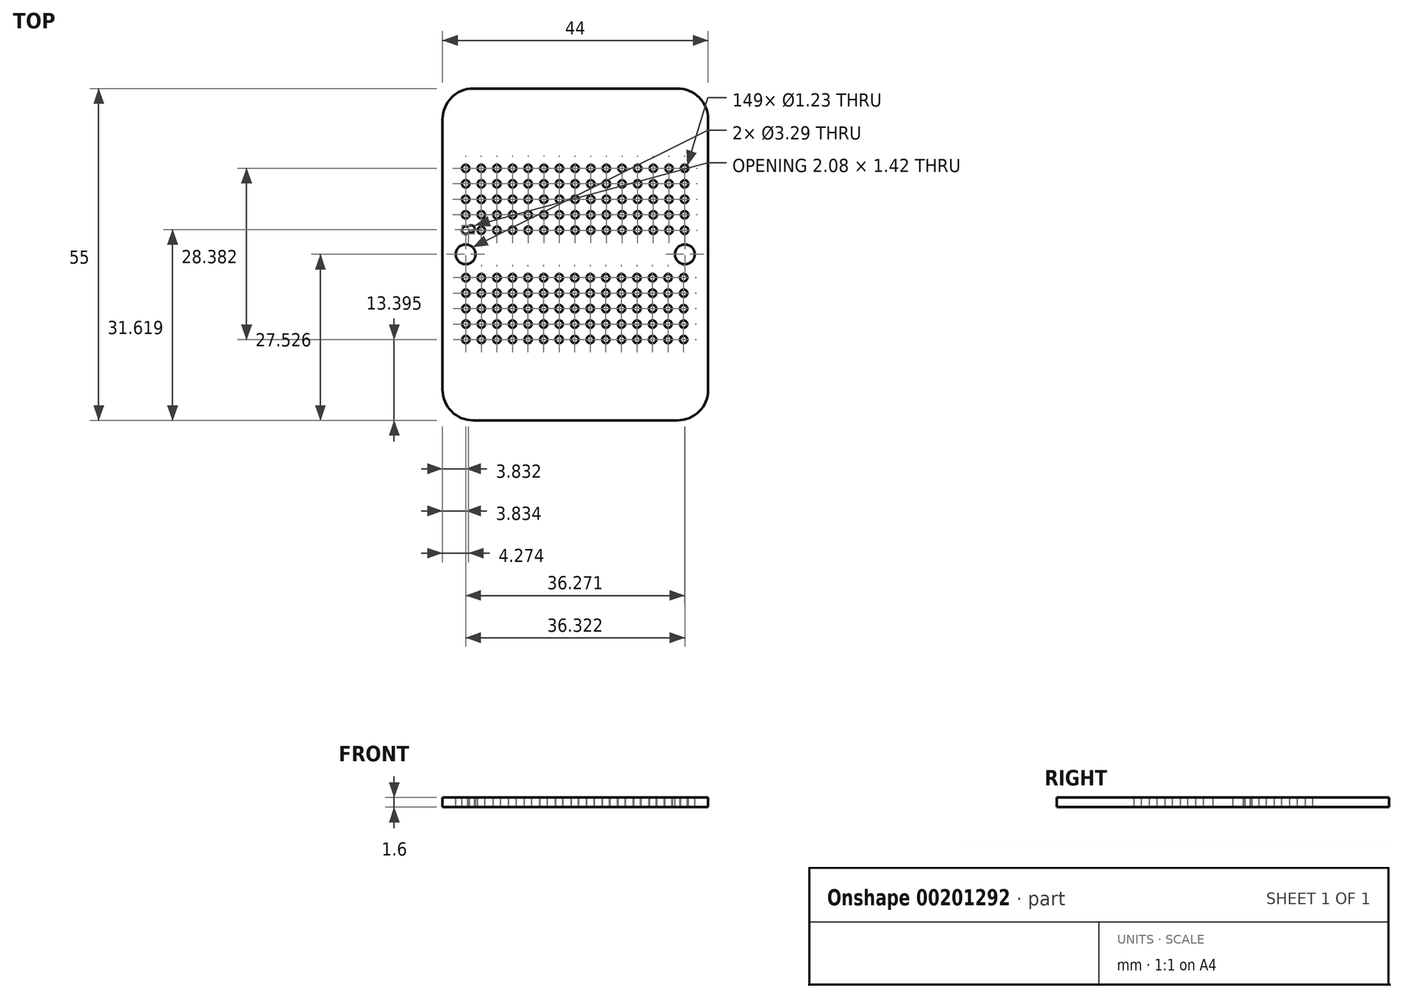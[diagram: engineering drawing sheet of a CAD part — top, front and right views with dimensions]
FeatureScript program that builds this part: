
annotation { "Feature Type Name" : "Feature", "Feature Type Description" : "" }
export const myFeature = defineFeature(function(context is Context, id is Id, definition is map)
    precondition{}
    {
        {
            var Q0;
            Q0=qCreatedBy(makeId("Top.planeOp"),FACE);
            var sketch = newSketch(context, id + "F0", { "sketchPlane" : qUnion([Q0])});
            skLineSegment(sketch, "E0.bottom", {"start": v(0, 0) * mm, "end": v(44, 0) * mm});
            skLineSegment(sketch, "E0.top", {"start": v(0, -55) * mm, "end": v(44, -55) * mm});
            skLineSegment(sketch, "E0.left", {"start": v(0, 0) * mm, "end": v(0, -55) * mm});
            skLineSegment(sketch, "E0.right", {"start": v(44, 0) * mm, "end": v(44, -55) * mm});
            skSolve(sketch);
        }
        {
            var Q0;
            Q0=makeQuery(id+"F0.imprint","IMPRINT",FACE,{"disambiguationData":[TD([[makeQuery(id+"F0.imprint","IMPRINT",EDGE,{"derivedFrom":sQuery(id+"F0.wireOp",EDGE,"E0.bottom")}),-1.0]])]});
            extrude(context, id + "F1", {"entities" : qUnion([Q0]), "depth" : 1.6 * mm});
        }
        {
            var Q0;
            Q0=makeQuery(id+"F1.opExtrude","SWEPT_EDGE",EDGE,{"disambiguationData":[OSD([sQuery(id+"F0.wireOp",EDGE,"E0.top"),sQuery(id+"F0.wireOp",EDGE,"E0.left")])]});
            var Q1;
            Q1=makeQuery(id+"F1.opExtrude","SWEPT_EDGE",EDGE,{"disambiguationData":[OSD([sQuery(id+"F0.wireOp",EDGE,"E0.top"),sQuery(id+"F0.wireOp",EDGE,"E0.right")])]});
            var Q2;
            Q2=makeQuery(id+"F1.opExtrude","SWEPT_EDGE",EDGE,{"disambiguationData":[OSD([sQuery(id+"F0.wireOp",EDGE,"E0.bottom"),sQuery(id+"F0.wireOp",EDGE,"E0.right")])]});
            var Q3;
            Q3=makeQuery(id+"F1.opExtrude","SWEPT_EDGE",EDGE,{"disambiguationData":[OSD([sQuery(id+"F0.wireOp",EDGE,"E0.bottom"),sQuery(id+"F0.wireOp",EDGE,"E0.left")])]});
            fillet(context, id + "F2", {"entities" : qUnion([Q0, Q1, Q2, Q3]), "radius" : 5.08 * mm, "tangentPropagation" : true, "allowEdgeOverflow" : false});
        }
        {
            var Q0;
            Q0=makeQuery(id+"F1.opExtrude","CAP_FACE",FACE,{"disambiguationData":[OSD([sQuery(id+"F0.wireOp",EDGE,"E0.bottom"),sQuery(id+"F0.wireOp",EDGE,"E0.top"),sQuery(id+"F0.wireOp",EDGE,"E0.left"),sQuery(id+"F0.wireOp",EDGE,"E0.right")])],"isStart":false});
            var sketch = newSketch(context, id + "F3", { "sketchPlane" : qUnion([Q0])});
            skCircle(sketch, "E1", {"center": v(3.83, -27.47) * mm, "radius": 1.65 * mm});
            skCircle(sketch, "E2.1.0.0", {"center": v(40.16, -27.47) * mm, "radius": 1.65 * mm});
            skLineSegment(sketch, "E2.direction1", {"start": v(3.83, -27.47) * mm, "end": v(40.16, -27.47) * mm, "construction": true});
            skCircle(sketch, "E3", {"center": v(3.83, -13.22) * mm, "radius": 0.61 * mm});
            skCircle(sketch, "E4.0.1.0", {"center": v(3.83, -15.79) * mm, "radius": 0.61 * mm});
            skCircle(sketch, "E4.0.2.0", {"center": v(3.83, -18.35) * mm, "radius": 0.61 * mm});
            skCircle(sketch, "E4.0.3.0", {"center": v(3.83, -20.92) * mm, "radius": 0.61 * mm});
            skCircle(sketch, "E4.0.4.0", {"center": v(3.83, -23.49) * mm, "radius": 0.61 * mm});
            skCircle(sketch, "E4.1.0.0", {"center": v(6.42, -13.22) * mm, "radius": 0.61 * mm});
            skCircle(sketch, "E4.1.1.0", {"center": v(6.42, -15.79) * mm, "radius": 0.61 * mm});
            skCircle(sketch, "E4.1.2.0", {"center": v(6.42, -18.35) * mm, "radius": 0.61 * mm});
            skCircle(sketch, "E4.1.3.0", {"center": v(6.42, -20.92) * mm, "radius": 0.61 * mm});
            skCircle(sketch, "E4.1.4.0", {"center": v(6.42, -23.49) * mm, "radius": 0.61 * mm});
            skCircle(sketch, "E4.2.0.0", {"center": v(9.01, -13.22) * mm, "radius": 0.61 * mm});
            skCircle(sketch, "E4.2.1.0", {"center": v(9.01, -15.79) * mm, "radius": 0.61 * mm});
            skCircle(sketch, "E4.2.2.0", {"center": v(9.01, -18.35) * mm, "radius": 0.61 * mm});
            skCircle(sketch, "E4.2.3.0", {"center": v(9.01, -20.92) * mm, "radius": 0.61 * mm});
            skCircle(sketch, "E4.2.4.0", {"center": v(9.01, -23.49) * mm, "radius": 0.61 * mm});
            skCircle(sketch, "E4.3.0.0", {"center": v(11.6, -13.22) * mm, "radius": 0.61 * mm});
            skCircle(sketch, "E4.3.1.0", {"center": v(11.6, -15.79) * mm, "radius": 0.61 * mm});
            skCircle(sketch, "E4.3.2.0", {"center": v(11.6, -18.35) * mm, "radius": 0.61 * mm});
            skCircle(sketch, "E4.3.3.0", {"center": v(11.6, -20.92) * mm, "radius": 0.61 * mm});
            skCircle(sketch, "E4.3.4.0", {"center": v(11.6, -23.49) * mm, "radius": 0.61 * mm});
            skCircle(sketch, "E4.4.0.0", {"center": v(14.2, -13.22) * mm, "radius": 0.61 * mm});
            skCircle(sketch, "E4.4.1.0", {"center": v(14.2, -15.79) * mm, "radius": 0.61 * mm});
            skCircle(sketch, "E4.4.2.0", {"center": v(14.2, -18.35) * mm, "radius": 0.61 * mm});
            skCircle(sketch, "E4.4.3.0", {"center": v(14.2, -20.92) * mm, "radius": 0.61 * mm});
            skCircle(sketch, "E4.4.4.0", {"center": v(14.2, -23.49) * mm, "radius": 0.61 * mm});
            skCircle(sketch, "E4.5.0.0", {"center": v(16.79, -13.22) * mm, "radius": 0.61 * mm});
            skCircle(sketch, "E4.5.1.0", {"center": v(16.79, -15.79) * mm, "radius": 0.61 * mm});
            skCircle(sketch, "E4.5.2.0", {"center": v(16.79, -18.35) * mm, "radius": 0.61 * mm});
            skCircle(sketch, "E4.5.3.0", {"center": v(16.79, -20.92) * mm, "radius": 0.61 * mm});
            skCircle(sketch, "E4.5.4.0", {"center": v(16.79, -23.49) * mm, "radius": 0.61 * mm});
            skCircle(sketch, "E4.6.0.0", {"center": v(19.38, -13.22) * mm, "radius": 0.61 * mm});
            skCircle(sketch, "E4.6.1.0", {"center": v(19.38, -15.79) * mm, "radius": 0.61 * mm});
            skCircle(sketch, "E4.6.2.0", {"center": v(19.38, -18.35) * mm, "radius": 0.61 * mm});
            skCircle(sketch, "E4.6.3.0", {"center": v(19.38, -20.92) * mm, "radius": 0.61 * mm});
            skCircle(sketch, "E4.6.4.0", {"center": v(19.38, -23.49) * mm, "radius": 0.61 * mm});
            skCircle(sketch, "E4.7.0.0", {"center": v(21.97, -13.22) * mm, "radius": 0.61 * mm});
            skCircle(sketch, "E4.7.1.0", {"center": v(21.97, -15.79) * mm, "radius": 0.61 * mm});
            skCircle(sketch, "E4.7.2.0", {"center": v(21.97, -18.35) * mm, "radius": 0.61 * mm});
            skCircle(sketch, "E4.7.3.0", {"center": v(21.97, -20.92) * mm, "radius": 0.61 * mm});
            skCircle(sketch, "E4.7.4.0", {"center": v(21.97, -23.49) * mm, "radius": 0.61 * mm});
            skCircle(sketch, "E4.8.0.0", {"center": v(24.56, -13.22) * mm, "radius": 0.61 * mm});
            skCircle(sketch, "E4.8.1.0", {"center": v(24.56, -15.79) * mm, "radius": 0.61 * mm});
            skCircle(sketch, "E4.8.2.0", {"center": v(24.56, -18.35) * mm, "radius": 0.61 * mm});
            skCircle(sketch, "E4.8.3.0", {"center": v(24.56, -20.92) * mm, "radius": 0.61 * mm});
            skCircle(sketch, "E4.8.4.0", {"center": v(24.56, -23.49) * mm, "radius": 0.61 * mm});
            skCircle(sketch, "E4.9.0.0", {"center": v(27.15, -13.22) * mm, "radius": 0.61 * mm});
            skCircle(sketch, "E4.9.1.0", {"center": v(27.15, -15.79) * mm, "radius": 0.61 * mm});
            skCircle(sketch, "E4.9.2.0", {"center": v(27.15, -18.35) * mm, "radius": 0.61 * mm});
            skCircle(sketch, "E4.9.3.0", {"center": v(27.15, -20.92) * mm, "radius": 0.61 * mm});
            skCircle(sketch, "E4.9.4.0", {"center": v(27.15, -23.49) * mm, "radius": 0.61 * mm});
            skCircle(sketch, "E4.10.0.0", {"center": v(29.74, -13.22) * mm, "radius": 0.61 * mm});
            skCircle(sketch, "E4.10.1.0", {"center": v(29.74, -15.79) * mm, "radius": 0.61 * mm});
            skCircle(sketch, "E4.10.2.0", {"center": v(29.74, -18.35) * mm, "radius": 0.61 * mm});
            skCircle(sketch, "E4.10.3.0", {"center": v(29.74, -20.92) * mm, "radius": 0.61 * mm});
            skCircle(sketch, "E4.10.4.0", {"center": v(29.74, -23.49) * mm, "radius": 0.61 * mm});
            skCircle(sketch, "E4.11.0.0", {"center": v(32.33, -13.22) * mm, "radius": 0.61 * mm});
            skCircle(sketch, "E4.11.1.0", {"center": v(32.33, -15.79) * mm, "radius": 0.61 * mm});
            skCircle(sketch, "E4.11.2.0", {"center": v(32.33, -18.35) * mm, "radius": 0.61 * mm});
            skCircle(sketch, "E4.11.3.0", {"center": v(32.33, -20.92) * mm, "radius": 0.61 * mm});
            skCircle(sketch, "E4.11.4.0", {"center": v(32.33, -23.49) * mm, "radius": 0.61 * mm});
            skCircle(sketch, "E4.12.0.0", {"center": v(34.92, -13.22) * mm, "radius": 0.61 * mm});
            skCircle(sketch, "E4.12.1.0", {"center": v(34.92, -15.79) * mm, "radius": 0.61 * mm});
            skCircle(sketch, "E4.12.2.0", {"center": v(34.92, -18.35) * mm, "radius": 0.61 * mm});
            skCircle(sketch, "E4.12.3.0", {"center": v(34.92, -20.92) * mm, "radius": 0.61 * mm});
            skCircle(sketch, "E4.12.4.0", {"center": v(34.92, -23.49) * mm, "radius": 0.61 * mm});
            skCircle(sketch, "E4.13.0.0", {"center": v(37.51, -13.22) * mm, "radius": 0.61 * mm});
            skCircle(sketch, "E4.13.1.0", {"center": v(37.51, -15.79) * mm, "radius": 0.61 * mm});
            skCircle(sketch, "E4.13.2.0", {"center": v(37.51, -18.35) * mm, "radius": 0.61 * mm});
            skCircle(sketch, "E4.13.3.0", {"center": v(37.51, -20.92) * mm, "radius": 0.61 * mm});
            skCircle(sketch, "E4.13.4.0", {"center": v(37.51, -23.49) * mm, "radius": 0.61 * mm});
            skCircle(sketch, "E4.14.0.0", {"center": v(40.1, -13.22) * mm, "radius": 0.61 * mm});
            skCircle(sketch, "E4.14.1.0", {"center": v(40.1, -15.79) * mm, "radius": 0.61 * mm});
            skCircle(sketch, "E4.14.2.0", {"center": v(40.1, -18.35) * mm, "radius": 0.61 * mm});
            skCircle(sketch, "E4.14.3.0", {"center": v(40.1, -20.92) * mm, "radius": 0.61 * mm});
            skCircle(sketch, "E4.14.4.0", {"center": v(40.1, -23.49) * mm, "radius": 0.61 * mm});
            skLineSegment(sketch, "E4.direction1", {"start": v(3.83, -13.22) * mm, "end": v(6.42, -13.22) * mm, "construction": true});
            skLineSegment(sketch, "E4.direction2", {"start": v(3.83, -13.22) * mm, "end": v(3.83, -15.79) * mm, "construction": true});
            skCircle(sketch, "E5", {"center": v(4.72, -23.28) * mm, "radius": 0.61 * mm});
            skCircle(sketch, "E6", {"center": v(3.86, -31.34) * mm, "radius": 0.61 * mm});
            skCircle(sketch, "E7.0.1.0", {"center": v(3.86, -33.9) * mm, "radius": 0.61 * mm});
            skCircle(sketch, "E7.0.2.0", {"center": v(3.86, -36.47) * mm, "radius": 0.61 * mm});
            skCircle(sketch, "E7.0.3.0", {"center": v(3.86, -39.04) * mm, "radius": 0.61 * mm});
            skCircle(sketch, "E7.0.4.0", {"center": v(3.86, -41.6) * mm, "radius": 0.61 * mm});
            skCircle(sketch, "E7.1.0.0", {"center": v(6.43, -31.34) * mm, "radius": 0.61 * mm});
            skCircle(sketch, "E7.1.1.0", {"center": v(6.43, -33.9) * mm, "radius": 0.61 * mm});
            skCircle(sketch, "E7.1.2.0", {"center": v(6.43, -36.47) * mm, "radius": 0.61 * mm});
            skCircle(sketch, "E7.1.3.0", {"center": v(6.43, -39.04) * mm, "radius": 0.61 * mm});
            skCircle(sketch, "E7.1.4.0", {"center": v(6.43, -41.6) * mm, "radius": 0.61 * mm});
            skCircle(sketch, "E7.2.0.0", {"center": v(9.01, -31.34) * mm, "radius": 0.61 * mm});
            skCircle(sketch, "E7.2.1.0", {"center": v(9.01, -33.9) * mm, "radius": 0.61 * mm});
            skCircle(sketch, "E7.2.2.0", {"center": v(9.01, -36.47) * mm, "radius": 0.61 * mm});
            skCircle(sketch, "E7.2.3.0", {"center": v(9.01, -39.04) * mm, "radius": 0.61 * mm});
            skCircle(sketch, "E7.2.4.0", {"center": v(9.01, -41.6) * mm, "radius": 0.61 * mm});
            skCircle(sketch, "E7.3.0.0", {"center": v(11.6, -31.34) * mm, "radius": 0.61 * mm});
            skCircle(sketch, "E7.3.1.0", {"center": v(11.6, -33.9) * mm, "radius": 0.61 * mm});
            skCircle(sketch, "E7.3.2.0", {"center": v(11.6, -36.47) * mm, "radius": 0.61 * mm});
            skCircle(sketch, "E7.3.3.0", {"center": v(11.6, -39.04) * mm, "radius": 0.61 * mm});
            skCircle(sketch, "E7.3.4.0", {"center": v(11.6, -41.6) * mm, "radius": 0.61 * mm});
            skCircle(sketch, "E7.4.0.0", {"center": v(14.17, -31.34) * mm, "radius": 0.61 * mm});
            skCircle(sketch, "E7.4.1.0", {"center": v(14.17, -33.9) * mm, "radius": 0.61 * mm});
            skCircle(sketch, "E7.4.2.0", {"center": v(14.17, -36.47) * mm, "radius": 0.61 * mm});
            skCircle(sketch, "E7.4.3.0", {"center": v(14.17, -39.04) * mm, "radius": 0.61 * mm});
            skCircle(sketch, "E7.4.4.0", {"center": v(14.17, -41.6) * mm, "radius": 0.61 * mm});
            skCircle(sketch, "E7.5.0.0", {"center": v(16.75, -31.34) * mm, "radius": 0.61 * mm});
            skCircle(sketch, "E7.5.1.0", {"center": v(16.75, -33.9) * mm, "radius": 0.61 * mm});
            skCircle(sketch, "E7.5.2.0", {"center": v(16.75, -36.47) * mm, "radius": 0.61 * mm});
            skCircle(sketch, "E7.5.3.0", {"center": v(16.75, -39.04) * mm, "radius": 0.61 * mm});
            skCircle(sketch, "E7.5.4.0", {"center": v(16.75, -41.6) * mm, "radius": 0.61 * mm});
            skCircle(sketch, "E7.6.0.0", {"center": v(19.32, -31.34) * mm, "radius": 0.61 * mm});
            skCircle(sketch, "E7.6.1.0", {"center": v(19.32, -33.9) * mm, "radius": 0.61 * mm});
            skCircle(sketch, "E7.6.2.0", {"center": v(19.32, -36.47) * mm, "radius": 0.61 * mm});
            skCircle(sketch, "E7.6.3.0", {"center": v(19.32, -39.04) * mm, "radius": 0.61 * mm});
            skCircle(sketch, "E7.6.4.0", {"center": v(19.32, -41.6) * mm, "radius": 0.61 * mm});
            skCircle(sketch, "E7.7.0.0", {"center": v(21.9, -31.34) * mm, "radius": 0.61 * mm});
            skCircle(sketch, "E7.7.1.0", {"center": v(21.9, -33.9) * mm, "radius": 0.61 * mm});
            skCircle(sketch, "E7.7.2.0", {"center": v(21.9, -36.47) * mm, "radius": 0.61 * mm});
            skCircle(sketch, "E7.7.3.0", {"center": v(21.9, -39.04) * mm, "radius": 0.61 * mm});
            skCircle(sketch, "E7.7.4.0", {"center": v(21.9, -41.6) * mm, "radius": 0.61 * mm});
            skCircle(sketch, "E7.8.0.0", {"center": v(24.48, -31.34) * mm, "radius": 0.61 * mm});
            skCircle(sketch, "E7.8.1.0", {"center": v(24.48, -33.9) * mm, "radius": 0.61 * mm});
            skCircle(sketch, "E7.8.2.0", {"center": v(24.48, -36.47) * mm, "radius": 0.61 * mm});
            skCircle(sketch, "E7.8.3.0", {"center": v(24.48, -39.04) * mm, "radius": 0.61 * mm});
            skCircle(sketch, "E7.8.4.0", {"center": v(24.48, -41.6) * mm, "radius": 0.61 * mm});
            skCircle(sketch, "E7.9.0.0", {"center": v(27.06, -31.34) * mm, "radius": 0.61 * mm});
            skCircle(sketch, "E7.9.1.0", {"center": v(27.06, -33.9) * mm, "radius": 0.61 * mm});
            skCircle(sketch, "E7.9.2.0", {"center": v(27.06, -36.47) * mm, "radius": 0.61 * mm});
            skCircle(sketch, "E7.9.3.0", {"center": v(27.06, -39.04) * mm, "radius": 0.61 * mm});
            skCircle(sketch, "E7.9.4.0", {"center": v(27.06, -41.6) * mm, "radius": 0.61 * mm});
            skCircle(sketch, "E7.10.0.0", {"center": v(29.64, -31.34) * mm, "radius": 0.61 * mm});
            skCircle(sketch, "E7.10.1.0", {"center": v(29.64, -33.9) * mm, "radius": 0.61 * mm});
            skCircle(sketch, "E7.10.2.0", {"center": v(29.64, -36.47) * mm, "radius": 0.61 * mm});
            skCircle(sketch, "E7.10.3.0", {"center": v(29.64, -39.04) * mm, "radius": 0.61 * mm});
            skCircle(sketch, "E7.10.4.0", {"center": v(29.64, -41.6) * mm, "radius": 0.61 * mm});
            skCircle(sketch, "E7.11.0.0", {"center": v(32.22, -31.34) * mm, "radius": 0.61 * mm});
            skCircle(sketch, "E7.11.1.0", {"center": v(32.22, -33.9) * mm, "radius": 0.61 * mm});
            skCircle(sketch, "E7.11.2.0", {"center": v(32.22, -36.47) * mm, "radius": 0.61 * mm});
            skCircle(sketch, "E7.11.3.0", {"center": v(32.22, -39.04) * mm, "radius": 0.61 * mm});
            skCircle(sketch, "E7.11.4.0", {"center": v(32.22, -41.6) * mm, "radius": 0.61 * mm});
            skCircle(sketch, "E7.12.0.0", {"center": v(34.8, -31.34) * mm, "radius": 0.61 * mm});
            skCircle(sketch, "E7.12.1.0", {"center": v(34.8, -33.9) * mm, "radius": 0.61 * mm});
            skCircle(sketch, "E7.12.2.0", {"center": v(34.8, -36.47) * mm, "radius": 0.61 * mm});
            skCircle(sketch, "E7.12.3.0", {"center": v(34.8, -39.04) * mm, "radius": 0.61 * mm});
            skCircle(sketch, "E7.12.4.0", {"center": v(34.8, -41.6) * mm, "radius": 0.61 * mm});
            skCircle(sketch, "E7.13.0.0", {"center": v(37.37, -31.34) * mm, "radius": 0.61 * mm});
            skCircle(sketch, "E7.13.1.0", {"center": v(37.37, -33.9) * mm, "radius": 0.61 * mm});
            skCircle(sketch, "E7.13.2.0", {"center": v(37.37, -36.47) * mm, "radius": 0.61 * mm});
            skCircle(sketch, "E7.13.3.0", {"center": v(37.37, -39.04) * mm, "radius": 0.61 * mm});
            skCircle(sketch, "E7.13.4.0", {"center": v(37.37, -41.6) * mm, "radius": 0.61 * mm});
            skCircle(sketch, "E7.14.0.0", {"center": v(39.95, -31.34) * mm, "radius": 0.61 * mm});
            skCircle(sketch, "E7.14.1.0", {"center": v(39.95, -33.9) * mm, "radius": 0.61 * mm});
            skCircle(sketch, "E7.14.2.0", {"center": v(39.95, -36.47) * mm, "radius": 0.61 * mm});
            skCircle(sketch, "E7.14.3.0", {"center": v(39.95, -39.04) * mm, "radius": 0.61 * mm});
            skCircle(sketch, "E7.14.4.0", {"center": v(39.95, -41.6) * mm, "radius": 0.61 * mm});
            skLineSegment(sketch, "E7.direction1", {"start": v(3.86, -31.34) * mm, "end": v(6.43, -31.34) * mm, "construction": true});
            skLineSegment(sketch, "E7.direction2", {"start": v(3.86, -31.34) * mm, "end": v(3.86, -33.9) * mm, "construction": true});
            skSolve(sketch);
        }
        {
            var Q0;
            Q0=makeQuery(id+"F3.imprint","IMPRINT",FACE,{"disambiguationData":[TD([[makeQuery(id+"F3.imprint","IMPRINT",EDGE,{"derivedFrom":sQuery(id+"F3.wireOp",EDGE,"E1")}),-1.0]])]});
            var Q1;
            Q1=sQuery(id+"F3.wireOp",EDGE,"E1");
            var Q2;
            Q2=sQuery(id+"F3.wireOp",EDGE,"E2.1.0.0");
            var Q3;
            Q3=makeQuery(id+"F1.opExtrude","CAP_FACE",FACE,{"disambiguationData":[OSD([sQuery(id+"F0.wireOp",EDGE,"E0.bottom"),sQuery(id+"F0.wireOp",EDGE,"E0.top"),sQuery(id+"F0.wireOp",EDGE,"E0.left"),sQuery(id+"F0.wireOp",EDGE,"E0.right")])],"isStart":true});
            extrude(context, id + "F4", {"entities" : qUnion([Q0]), "operationType" : NewBodyOperationType.INTERSECT, "surfaceEntities" : qUnion([Q1, Q2]), "endBound" : BoundingType.UP_TO_SURFACE, "oppositeDirection" : true, "endBoundEntityFace" : qUnion([Q3]), "depth" : 25.4 * mm});
        }
    });
